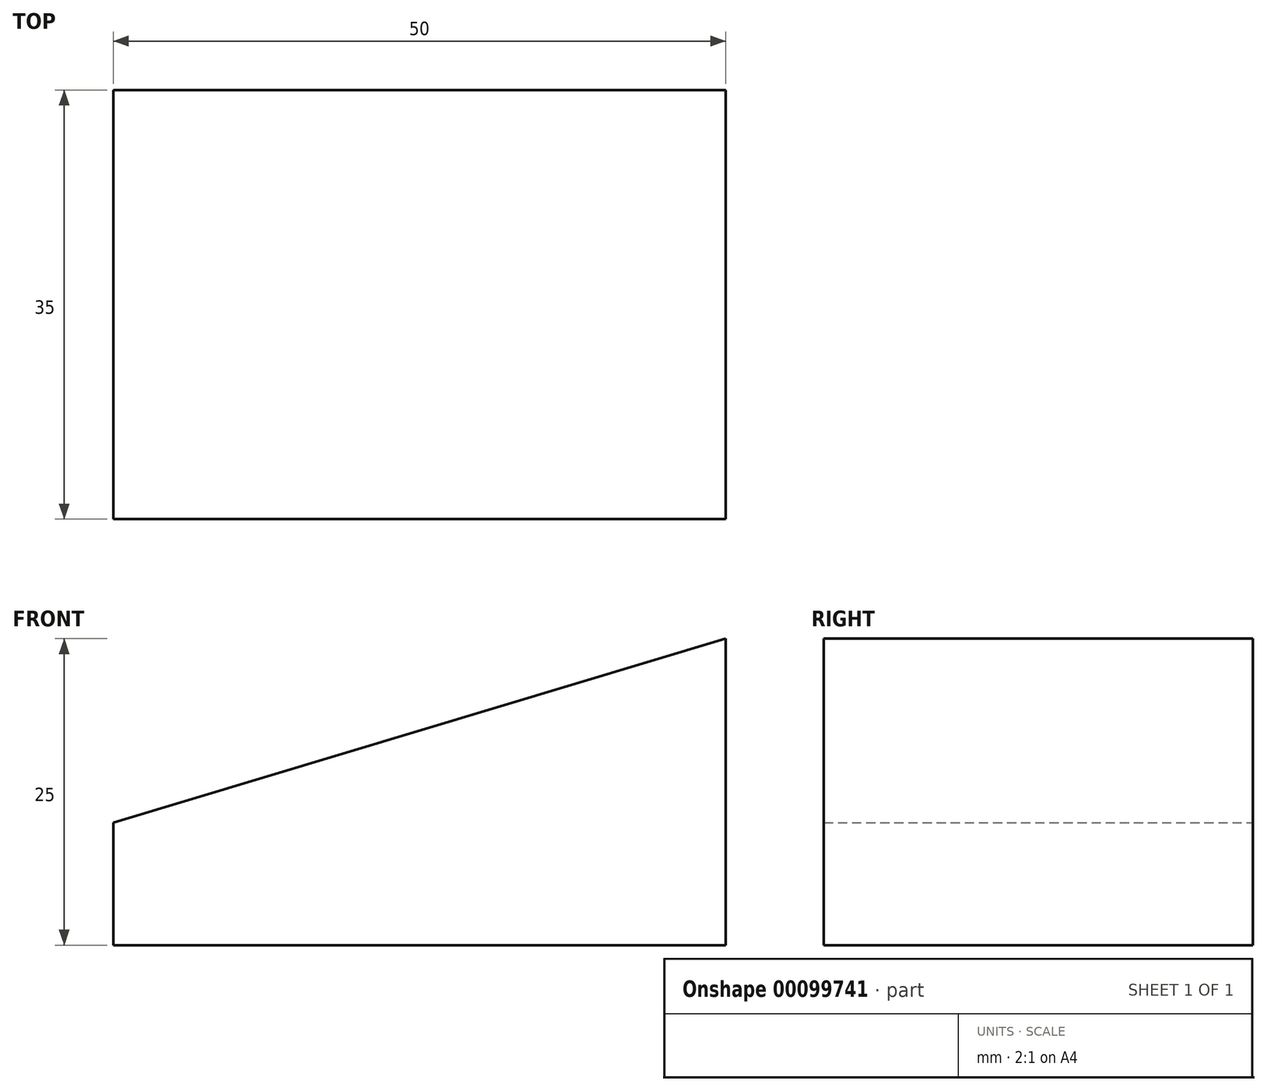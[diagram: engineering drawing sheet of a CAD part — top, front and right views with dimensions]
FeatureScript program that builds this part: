
annotation { "Feature Type Name" : "Feature", "Feature Type Description" : "" }
export const myFeature = defineFeature(function(context is Context, id is Id, definition is map)
    precondition{}
    {
        {
            var Q0;
            Q0=qCreatedBy(makeId("Front.planeOp"),FACE);
            var sketch = newSketch(context, id + "F0", { "sketchPlane" : qUnion([Q0])});
            skLineSegment(sketch, "E0.bottom", {"start": v(0, 0) * mm, "end": v(-50, 0) * mm});
            skLineSegment(sketch, "E0.top", {"start": v(0, 25) * mm, "end": v(-50, 25) * mm});
            skLineSegment(sketch, "E0.left", {"start": v(0, 0) * mm, "end": v(0, 25) * mm});
            skLineSegment(sketch, "E0.right", {"start": v(-50, 0) * mm, "end": v(-50, 25) * mm});
            skSolve(sketch);
        }
        {
            var Q0;
            Q0 = qSketchRegion(id + "F0", true);
            var Q1;
            Q1=makeQuery(id+"F0.imprint","IMPRINT",FACE,{"disambiguationData":[TD([[makeQuery(id+"F0.imprint","IMPRINT",EDGE,{"derivedFrom":sQuery(id+"F0.wireOp",EDGE,"E0.bottom")}),-1.0]])]});
            extrude(context, id + "F1", {"entities" : qUnion([Q0, Q1]), "depth" : 35 * mm});
        }
        {
            var Q0;
            Q0=makeQuery(id+"F1.opExtrude","SWEPT_EDGE",EDGE,{"disambiguationData":[OSD([sQuery(id+"F0.wireOp",EDGE,"E0.top"),sQuery(id+"F0.wireOp",EDGE,"E0.right")])]});
            chamfer(context, id + "F2", {"entities" : qUnion([Q0]), "chamferType" : ChamferType.TWO_OFFSETS, "width1" : 15 * mm, "oppositeDirection" : false, "width2" : 50 * mm, "tangentPropagation" : true});
        }
    });
